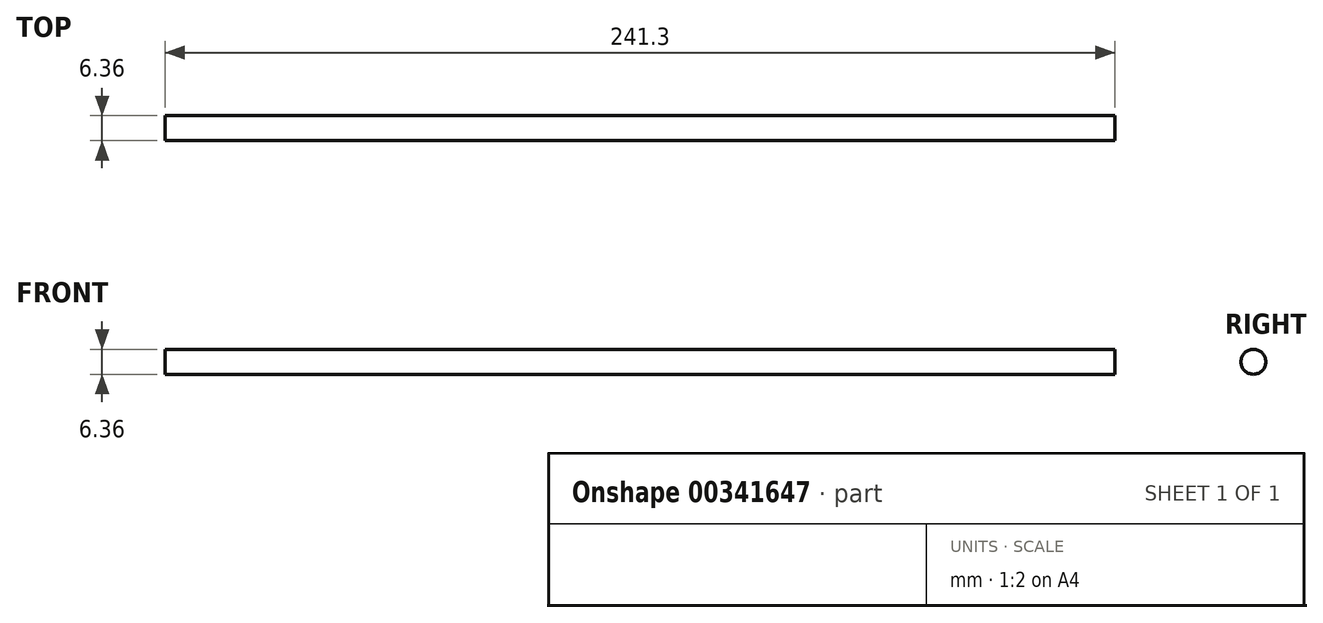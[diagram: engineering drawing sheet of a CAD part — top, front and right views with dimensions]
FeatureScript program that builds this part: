
annotation { "Feature Type Name" : "Feature", "Feature Type Description" : "" }
export const myFeature = defineFeature(function(context is Context, id is Id, definition is map)
    precondition{}
    {
        {
            var Q0;
            Q0=qCreatedBy(makeId("Right.planeOp"),FACE);
            var sketch = newSketch(context, id + "F0", { "sketchPlane" : qUnion([Q0])});
            skCircle(sketch, "E0", {"center": v(0, 0) * mm, "radius": 3.18 * mm});
            skSolve(sketch);
        }
        {
            var Q0;
            Q0 = qSketchRegion(id + "F0", true);
            extrude(context, id + "F1", {"entities" : qUnion([Q0]), "depth" : 241.3 * mm});
        }
    });
